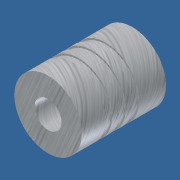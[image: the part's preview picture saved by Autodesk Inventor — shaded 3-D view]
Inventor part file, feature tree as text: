
AUTODESK INVENTOR PART (.ipt)
format: ipt  version: 2012 SP1 (Build 160190100, 190)  size: 133,120 bytes
history: native  units: in
note: dims shown in document units (in); Inventor stores cm internally (conversion verified against a paired STEP export)
features: extrude x3, sketch x3, plane x1, pattern_linear x1
ambient origin geometry x8: Origin, YZ Plane, XZ Plane, XY Plane, X Axis, Y Axis, Z Axis, Center Point
bodies: Solid1 (feature_tree)
feature tree (8):
  extrude  "Extrusion1"  Depth=0.7874in
  extrude  "Extrusion2"  Depth=0.315in
  plane  "Work Plane2"
  extrude  "Extrusion5"  [1 undecoded]
  pattern_linear  "Rectangular Pattern1"  Spacing1=0.8661in  [1 undecoded]
  sketch  "Sketch1"  dims[d0=0.1969in d1=0.7874in]
  sketch  "Sketch2"  dims[d2=0.9843in d3=0.0in d4=0.315in]
  sketch  "Sketch6"  dims[d5=0.375in d6=0.0in d10=-0.3125in d11=0.8661in d14=0.748in d15=0.0787in d16=0.0in d17=1.1811in d19=0.1575in]
note: 2 required parameter values undecoded (feature->parameter linkage not recoverable at this tier; creation-order binding heuristic only, values carry confidence <= 0.55)
